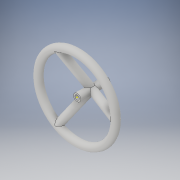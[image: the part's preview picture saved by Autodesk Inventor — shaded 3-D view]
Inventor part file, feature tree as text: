
AUTODESK INVENTOR PART (.ipt)
format: ipt  version: 2019 (Build 230136000, 136)  size: 197,120 bytes
history: native  units: mm
features: sketch x8, plane x5, other x3, sweep x2, hole x2, pattern_circular x1, extrude x1
ambient origin geometry x8: Origin, YZ Plane, XZ Plane, XY Plane, X Axis, Y Axis, Z Axis, Center Point
bodies: Solid1 (feature_tree)
feature tree (22):
  sketch  "Sketch1"  dims[d0=105.0mm d1=10.0mm]
  plane  "Work Plane1"
  sweep  "Sweep1"
  sketch  "Sketch3"  dims[d5=10.0mm]
  plane  "Work Plane2"
  sketch  "Sketch4"  dims[d6=0.0mm d7=0.0mm d8=30.0mm d9=360.0deg]
  plane  "Work Plane3"
  sweep  "Sweep2"
  pattern_circular  "Circular Pattern1"  Count=3 Angle=360.0deg
  other  "Work Point1"
  plane  "Work Plane4"
  extrude  "Extrusion1"  Depth=10.0mm TaperAngle=0.0deg
  plane  "Work Plane5"
  hole  "Hole1"  [1 undecoded]
  other  "Work Point2"
  hole  "Hole2"  [1 undecoded]
  sketch  "Sketch2"  dims[d2=0.0mm d3=0.0mm d4=20.0mm]
  sketch  "Sketch5"  dims[d11=10.0mm d12=40.0mm d13=0.0mm]
  other  "Work Axis1"
  sketch  "Sketch6"  dims[d14=5.0mm d15=6.0mm d16=4.0mm d17=2.0mm d18=90.0deg d19=8.0mm d20=20.594885mm]
  sketch  "Sketch7"  dims[d21=6.0mm d22=6.0mm d23=4.0mm d24=2.0mm d25=90.0deg d26=8.0mm d27=20.594885mm d28=4.0mm]
  sketch  "Sketch8"
note: 2 required parameter values undecoded (feature->parameter linkage not recoverable at this tier; creation-order binding heuristic only, values carry confidence <= 0.55)
